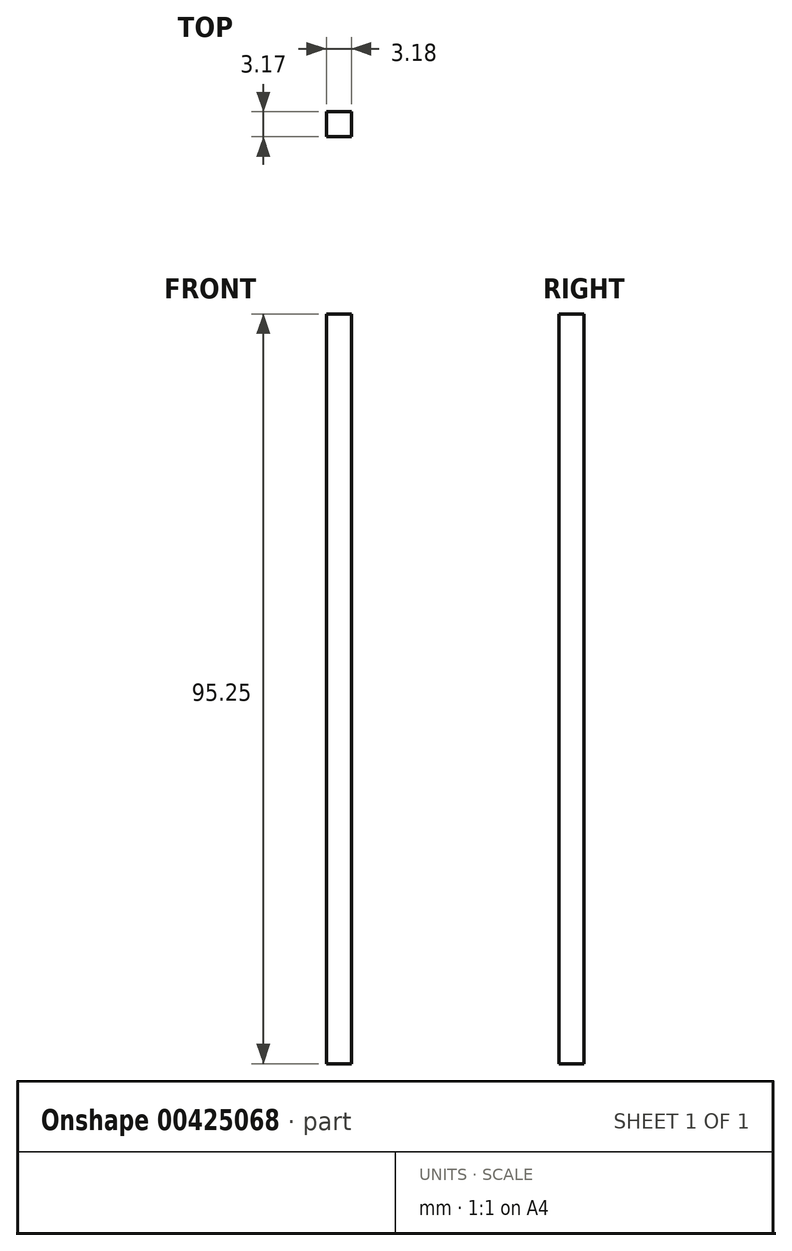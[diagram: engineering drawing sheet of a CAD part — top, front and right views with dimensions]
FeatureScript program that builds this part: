
annotation { "Feature Type Name" : "Feature", "Feature Type Description" : "" }
export const myFeature = defineFeature(function(context is Context, id is Id, definition is map)
    precondition{}
    {
        {
            var Q0;
            Q0=qCreatedBy(makeId("Front.planeOp"),FACE);
            var sketch = newSketch(context, id + "F0", { "sketchPlane" : qUnion([Q0])});
            skLineSegment(sketch, "E0", {"start": v(-16.75, 32.4) * mm, "end": v(-16.75, -62.86) * mm});
            skLineSegment(sketch, "E1", {"start": v(-16.75, -62.86) * mm, "end": v(-13.57, -62.86) * mm});
            skLineSegment(sketch, "E2", {"start": v(-13.57, -62.86) * mm, "end": v(-13.57, 32.4) * mm});
            skLineSegment(sketch, "E3", {"start": v(-13.57, 32.4) * mm, "end": v(-16.75, 32.4) * mm});
            skSolve(sketch);
        }
        {
            var Q0;
            Q0=makeQuery(id+"F0.imprint","IMPRINT",FACE,{"disambiguationData":[TD([[makeQuery(id+"F0.imprint","IMPRINT",EDGE,{"derivedFrom":sQuery(id+"F0.wireOp",EDGE,"E0")}),1.0]])]});
            extrude(context, id + "F1", {"entities" : qUnion([Q0]), "depth" : 3.17 * mm});
        }
    });
